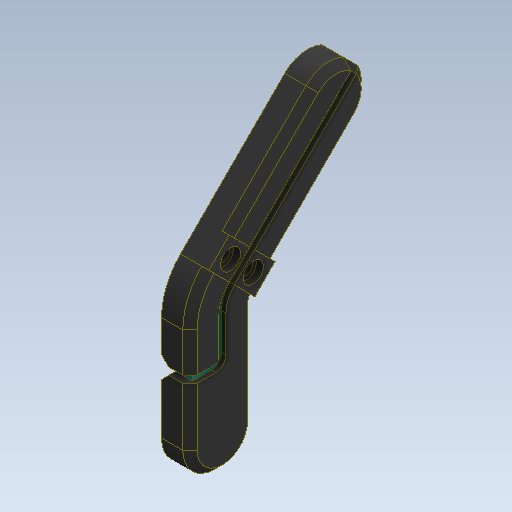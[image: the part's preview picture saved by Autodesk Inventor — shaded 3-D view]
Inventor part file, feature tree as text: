
AUTODESK INVENTOR PART (.ipt)
format: ipt  version: 2020 (Build 240168000, 168)  size: 402,944 bytes
history: native  units: in
note: dims shown in document units (in); Inventor stores cm internally (conversion verified against a paired STEP export)
features: sketch x30, other x7, plane x4
ambient origin geometry x8: Origin, YZ Plane, XZ Plane, XY Plane, X Axis, Y Axis, Z Axis, Center Point
bodies: Solid2 (feature_tree), Solid3 (feature_tree), Solid1 (feature_tree), Solid4 (feature_tree)
feature tree (41):
  other  "PatellaTop.ipt"
  other  "Solid1::PatellaTop.ipt"
  other  "Solid4::PatellaTop.ipt"
  other  "Solid5::PatellaTop.ipt"
  other  "Solid2::PatellaTop.ipt"
  other  "Solid3::PatellaTop.ipt"
  other  "TaggingFeature1"
  sketch  "Sketch1"  dims[d0=0.3937in]
  sketch  "Sketch2"
  sketch  "Sketch3"
  sketch  "Sketch4"
  sketch  "Sketch5"
  sketch  "Sketch12"
  sketch  "Sketch14"
  sketch  "Sketch15"
  sketch  "Sketch16"
  sketch  "Sketch17"
  sketch  "Sketch19"
  sketch  "Sketch22"
  sketch  "Sketch23"
  sketch  "Sketch24"
  sketch  "Sketch25"
  sketch  "Sketch26"
  sketch  "Sketch27"
  sketch  "Sketch28"
  sketch  "Sketch29"
  sketch  "Sketch30"
  sketch  "Sketch31"
  sketch  "Sketch32"
  sketch  "Sketch33"
  sketch  "Sketch39"
  sketch  "Sketch40"
  sketch  "Sketch44"
  sketch  "Sketch45"
  sketch  "Sketch46"
  sketch  "Sketch48"
  sketch  "Sketch49"
  plane  "Work Plane1"
  plane  "Work Plane2"
  plane  "Work Plane3"
  plane  "Work Plane4"
